# Revit family: 0005352
name_source: partatom
category: Lighting Fixtures
revit_build: Autodesk Revit 2017 (Build: 20190507_1515(x64)
units: mm (PartAtom-declared; Revit-internal decimal feet)

## family parameters
Cut with Voids When Loaded = No
Host = Face
Light Source = Yes
OmniClass Number = 23.80.70.00
OmniClass Title = Lighting
Part Type = Normal
Room Calculation Point = No
Round Connector Dimension = Use Diameter
Shared = No

## types (1)
- 0005352 OBICO IP65 FIRE 740LM 2CCT DIM WHT
    Apparent Load = 9 VA
    Assembly Code = D5020200
    AssetType = Fixed
    ClassificationName = Uniclass2015
    ClassificationValue = EF_70_80
    Color Filter = 16777215
    Cost = 0 $
    Default Elevation = 1219 mm
    Description = Integrated LED fire rated recessed spotlight, 2-axis adjustable (horizontal rotation 360°, vertical tilt 30°) RAL9016 white bezel colour, two temperature light colors selectable: 3000K, 4000K. Lumen output 740lm (4000K), 8.5W, dimmable trailing/leading edge, 38° degree beam angle, steel body, low profile 54mm recessed depth, IP65 frontal degree, IK03, loop-in/loop-out terminals for fast wiring, 96mm bezel diameter, 83mm cutout, clear lens. Additional chrome bezel ring included in the packaging. Designed and tested to meet Fire Rating Standards (30, 60, 90-minute fire rated ceilings) for safety and reassurance: BS 476-21:1987. Fire rated model tested for 30 & 60 minute I-Joist ceiling system (TRUfloorsystems® by Staircraft). Lifetime: 50.000 hours at L70. Energy Class: A++, A+, A.
    Dimming Lamp Color Temperature Shift = <None>
    DocumentationLiterature = http://www.sylvania-lighting.com
    ElectricShockClassification = Class II
    Emit Shape Visible in Rendering = No
    Emit from Circle Diameter = 610 mm
    IfcExportAs = IfcLightFixtureType
    IfcExportType = IfcLightFixtureType
    ImpactProtectionIndex = IK03
    IngressProtection = IP65/20
    Keynote = 16500
    Lamp = LED
    LampColourRenderingIndex = 80
    LampColourTemperature = 4000 K
    LampMacAdamStep = 6
    LampNominalLuminous = 720 lm
    LampsType = LED
    LuminousEfficacy = 84 lm/W
    Manufacturer = Feilo Sylvania
    ManufacturerName = Feilo Sylvania
    Material = aluminium housing, pc polycarbonate diffuser
    Material_1_SYL = Default
    Material_2_SYL = <By Category>
    Material_3_SYL = <By Category>
    Material_4_SYL = <By Category>
    Model = OBICO IP65 FIRE 740LM 2CCT DIM ADJ WHT
    ModelNumber = 0005352
    ModelReference = OBICO IP65 FIRE 740LM 2CCT DIM ADJ WHT
    Name = OBICO IP65 FIRE 740LM 2CCT DIM ADJ WHT
    NominalDepth = 96 mm  [stored 0.314961 ft]
    NominalHeight = 54 mm  [stored 0.177165 ft]
    NominalLength = 117 mm  [stored 0.383858 ft]
    Photometric Web File = 0005352.ies
    PowerConsumption = 8.5 W
    PowerFactor = 0.9
    Tilt Angle = -90.00°
    Type Image = <None>
    TypeName = OBICO IP65 FIRE 740LM 2CCT DIM ADJ WHT
    URL = http://www.sylvania-lighting.com
    Voltage = 0 V
    Weight = 2.1 kg

note: [stored X ft] marks values corroborated as IEEE doubles in the binary element streams (Revit-internal decimal feet)

## geometry (parser evidence)
native form markers: Sweep x3
no freeform markers — native parametric forms only
